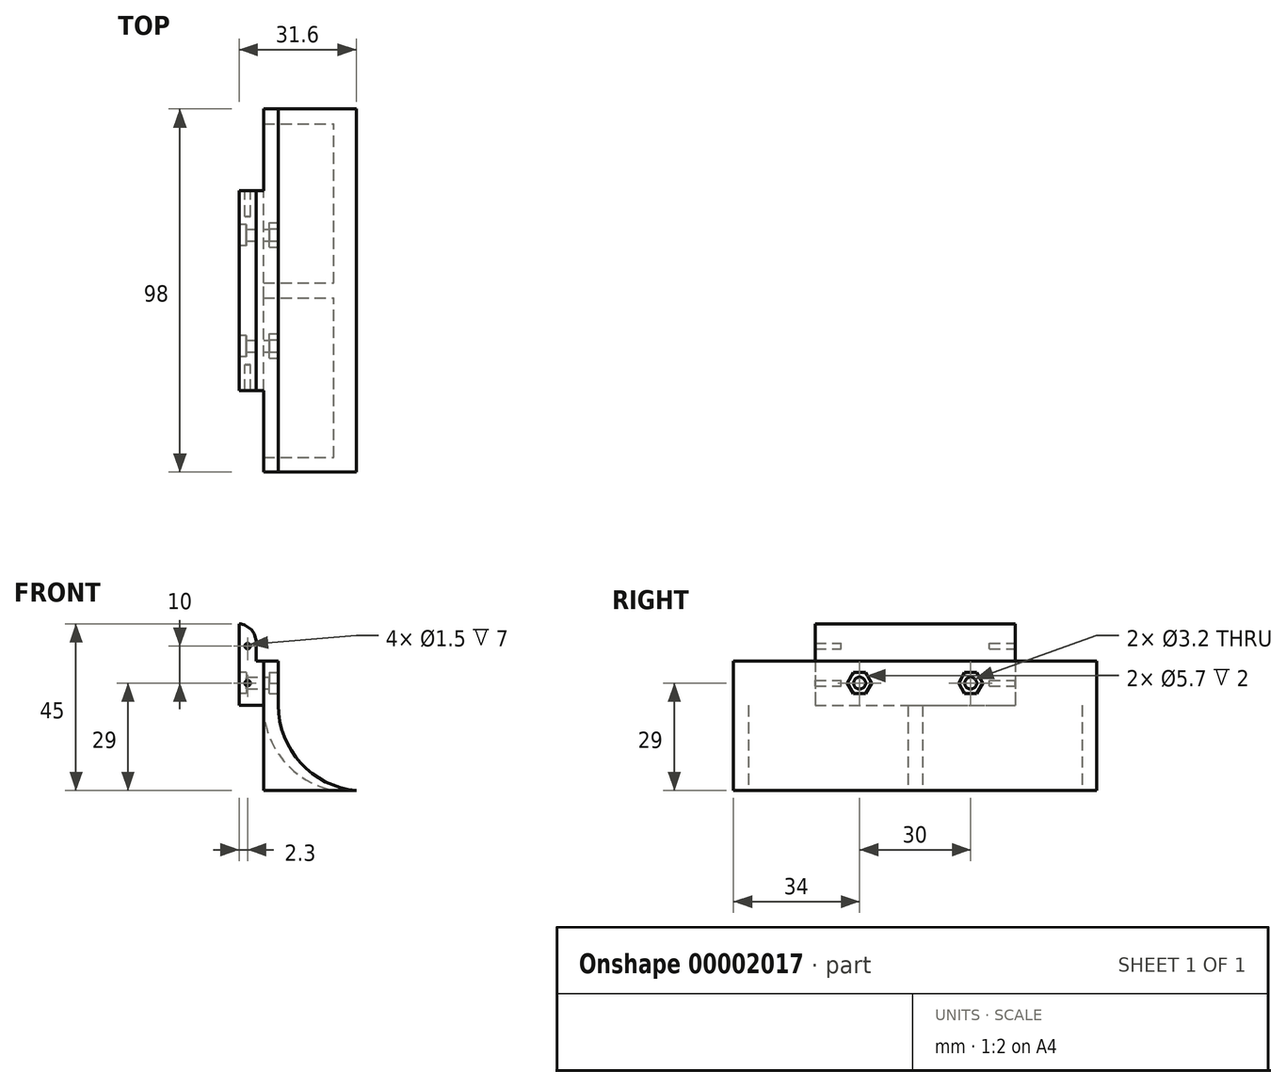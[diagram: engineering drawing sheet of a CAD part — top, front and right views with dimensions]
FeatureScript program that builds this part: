
annotation { "Feature Type Name" : "Feature", "Feature Type Description" : "" }
export const myFeature = defineFeature(function(context is Context, id is Id, definition is map)
    precondition{}
    {
        {
            var Q0;
            Q0=qCreatedBy(makeId("Front.planeOp"),FACE);
            var sketch = newSketch(context, id + "F0", { "sketchPlane" : qUnion([Q0])});
            skLineSegment(sketch, "E0", {"start": v(0, 0) * mm, "end": v(27, 0) * mm, "construction": true});
            skLineSegment(sketch, "E1", {"start": v(0, 0) * mm, "end": v(0, 35) * mm, "construction": true});
            skLineSegment(sketch, "E2", {"start": v(0, 35) * mm, "end": v(0, 45) * mm});
            skLineSegment(sketch, "E3", {"start": v(0, 45) * mm, "end": v(-4.6, 45) * mm});
            skLineSegment(sketch, "E4", {"start": v(-4.6, 45) * mm, "end": v(-4.6, 23) * mm});
            skLineSegment(sketch, "E5", {"start": v(-4.6, 23) * mm, "end": v(0, 23) * mm});
            skLineSegment(sketch, "E6", {"start": v(-2.3, 45) * mm, "end": v(-2.3, 23) * mm, "construction": true});
            skCircle(sketch, "E7", {"center": v(-2.3, 39) * mm, "radius": 0.75 * mm});
            skPoint(sketch, "E8", {"position": v(-2.3, 34) * mm});
            skCircle(sketch, "E9", {"center": v(-2.3, 29) * mm, "radius": 0.75 * mm});
            skLineSegment(sketch, "E10", {"start": v(0, 23) * mm, "end": v(6, 23) * mm});
            skLineSegment(sketch, "E11", {"start": v(6, 23) * mm, "end": v(6, 35) * mm});
            skLineSegment(sketch, "E12", {"start": v(6, 35) * mm, "end": v(0, 35) * mm});
            skArc(sketch, "E13", {"start": v(6, 23) * mm, "mid": v(12.04, 7.43) * mm, "end": v(27, 0) * mm});
            skLineSegment(sketch, "E14", {"start": v(2, 35) * mm, "end": v(2, 23) * mm});
            skLineSegment(sketch, "E15", {"start": v(2, 23) * mm, "end": v(2, 0) * mm});
            skLineSegment(sketch, "E16", {"start": v(2, 0) * mm, "end": v(27, 0) * mm});
            skArc(sketch, "E17", {"start": v(2, 23) * mm, "mid": v(7.36, 8.08) * mm, "end": v(21, 0) * mm});
            skSolve(sketch);
        }
        {
            var Q0;
            {var subQ2=sQuery(id+"F0.wireOp",EDGE,"E2");Q0=makeQuery(id+"F0.imprint","IMPRINT",FACE,{"disambiguationData":[TD([[makeQuery(id+"F0.imprint","IMPRINT",EDGE,{"derivedFrom":subQ2}),1.0]])]});}
            extrude(context, id + "F1", {"entities" : qUnion([Q0]), "endBound" : BoundingType.SYMMETRIC, "depth" : (27 * 2) * mm});
        }
        {
            var Q0;
            Q0=makeQuery(id+"F1.opExtrude","SWEPT_EDGE",EDGE,{"disambiguationData":[OSD([sQuery(id+"F0.wireOp",EDGE,"E2"),sQuery(id+"F0.wireOp",EDGE,"E3")])]});
            fillet(context, id + "F2", {"entities" : qUnion([Q0]), "radius" : 5 * mm, "tangentPropagation" : true, "allowEdgeOverflow" : false});
        }
        {
            var Q0;
            {var subQ2=sQuery(id+"F0.wireOp",EDGE,"E13");Q0=makeQuery(id+"F0.imprint","IMPRINT",FACE,{"disambiguationData":[TD([[makeQuery(id+"F0.imprint","IMPRINT",EDGE,{"derivedFrom":subQ2}),-1.0]])]});}
            var Q1;
            {var subQ2=sQuery(id+"F0.wireOp",EDGE,"E11");Q1=makeQuery(id+"F0.imprint","IMPRINT",FACE,{"disambiguationData":[TD([[makeQuery(id+"F0.imprint","IMPRINT",EDGE,{"derivedFrom":subQ2}),1.0]])]});}
            var Q2;
            {var subQ2=sQuery(id+"F0.wireOp",EDGE,"E15");Q2=makeQuery(id+"F0.imprint","IMPRINT",FACE,{"disambiguationData":[TD([[makeQuery(id+"F0.imprint","IMPRINT",EDGE,{"derivedFrom":subQ2}),1.0]])]});}
            extrude(context, id + "F3", {"entities" : qUnion([Q0, Q1, Q2]), "endBound" : BoundingType.SYMMETRIC, "depth" : 98 * mm});
        }
        {
            var Q0;
            {var subQ2=sQuery(id+"F0.wireOp",EDGE,"E15");Q0=makeQuery(id+"F0.imprint","IMPRINT",FACE,{"disambiguationData":[TD([[makeQuery(id+"F0.imprint","IMPRINT",EDGE,{"derivedFrom":subQ2}),1.0]])]});}
            extrude(context, id + "F4", {"entities" : qUnion([Q0]), "operationType" : NewBodyOperationType.REMOVE, "endBound" : BoundingType.SYMMETRIC, "depth" : 90 * mm});
        }
        {
            var Q0;
            Q0=makeQuery(id+"F0.imprint","IMPRINT",FACE,{"disambiguationData":[TD([[makeQuery(id+"F0.imprint","IMPRINT",EDGE,{"derivedFrom":sQuery(id+"F0.wireOp",EDGE,"E9")}),1.0]])]});
            var Q1;
            Q1=makeQuery(id+"F0.imprint","IMPRINT",FACE,{"disambiguationData":[TD([[makeQuery(id+"F0.imprint","IMPRINT",EDGE,{"derivedFrom":sQuery(id+"F0.wireOp",EDGE,"E7")}),1.0]])]});
            extrude(context, id + "F5", {"entities" : qUnion([Q0, Q1]), "operationType" : NewBodyOperationType.ADD, "endBound" : BoundingType.SYMMETRIC, "depth" : 40 * mm});
        }
        {
            var Q0;
            Q0=makeQuery(id+"F3.opExtrude","SWEPT_FACE",FACE,{"disambiguationData":[OSD([sQuery(id+"F0.wireOp",EDGE,"E11")])]});
            var sketch = newSketch(context, id + "F6", { "sketchPlane" : qUnion([Q0])});
            skLineSegment(sketch, "E18", {"start": v(0, 35) * mm, "end": v(0, 23) * mm, "construction": true});
            skPoint(sketch, "E19", {"position": v(0, 29) * mm});
            skCircle(sketch, "E20", {"center": v(-15, 29) * mm, "radius": 1.6 * mm});
            skCircle(sketch, "E21", {"center": v(15, 29) * mm, "radius": 1.6 * mm});
            skSolve(sketch);
        }
        {
            var Q0;
            Q0=makeQuery(id+"F6.imprint","IMPRINT",FACE,{"disambiguationData":[TD([[makeQuery(id+"F6.imprint","IMPRINT",EDGE,{"derivedFrom":sQuery(id+"F6.wireOp",EDGE,"E20")}),1.0]])]});
            var Q1;
            Q1=makeQuery(id+"F6.imprint","IMPRINT",FACE,{"disambiguationData":[TD([[makeQuery(id+"F6.imprint","IMPRINT",EDGE,{"derivedFrom":sQuery(id+"F6.wireOp",EDGE,"E21")}),1.0]])]});
            extrude(context, id + "F7", {"entities" : qUnion([Q0, Q1]), "operationType" : NewBodyOperationType.REMOVE, "endBound" : BoundingType.THROUGH_ALL, "oppositeDirection" : true, "depth" : 25 * mm});
        }
        {
            var Q0;
            {var subQ2=sQuery(id+"F0.wireOp",EDGE,"E15");Q0=makeQuery(id+"F0.imprint","IMPRINT",FACE,{"disambiguationData":[TD([[makeQuery(id+"F0.imprint","IMPRINT",EDGE,{"derivedFrom":subQ2}),1.0]])]});}
            extrude(context, id + "F8", {"entities" : qUnion([Q0]), "operationType" : NewBodyOperationType.ADD, "endBound" : BoundingType.SYMMETRIC, "depth" : 4 * mm});
        }
        {
            var Q0;
            Q0=makeQuery(id+"F3.opExtrude","SWEPT_FACE",FACE,{"disambiguationData":[OSD([sQuery(id+"F0.wireOp",EDGE,"E11")])]});
            var sketch = newSketch(context, id + "F9", { "sketchPlane" : qUnion([Q0])});
            skCircle(sketch, "E22.cCircle", {"center": v(-15, 29) * mm, "radius": 2.85 * mm, "construction": true});
            skLineSegment(sketch, "E22.0", {"start": v(-13.35, 31.85) * mm, "end": v(-11.7, 29) * mm});
            skLineSegment(sketch, "E22.1", {"start": v(-11.7, 29) * mm, "end": v(-13.35, 26.15) * mm});
            skLineSegment(sketch, "E22.2", {"start": v(-13.35, 26.15) * mm, "end": v(-16.65, 26.15) * mm});
            skLineSegment(sketch, "E22.3", {"start": v(-16.65, 26.15) * mm, "end": v(-18.3, 29) * mm});
            skLineSegment(sketch, "E22.4", {"start": v(-18.3, 29) * mm, "end": v(-16.65, 31.85) * mm});
            skLineSegment(sketch, "E22.5", {"start": v(-16.65, 31.85) * mm, "end": v(-13.35, 31.85) * mm});
            skPoint(sketch, "E22.0.midPoint", {"position": v(-12.53, 30.43) * mm});
            skCircle(sketch, "E23.cCircle", {"center": v(15, 29) * mm, "radius": 2.85 * mm, "construction": true});
            skLineSegment(sketch, "E23.0", {"start": v(16.65, 31.85) * mm, "end": v(18.3, 29) * mm});
            skLineSegment(sketch, "E23.1", {"start": v(18.3, 29) * mm, "end": v(16.65, 26.15) * mm});
            skLineSegment(sketch, "E23.2", {"start": v(16.65, 26.15) * mm, "end": v(13.35, 26.15) * mm});
            skLineSegment(sketch, "E23.3", {"start": v(13.35, 26.15) * mm, "end": v(11.7, 29) * mm});
            skLineSegment(sketch, "E23.4", {"start": v(11.7, 29) * mm, "end": v(13.35, 31.85) * mm});
            skLineSegment(sketch, "E23.5", {"start": v(13.35, 31.85) * mm, "end": v(16.65, 31.85) * mm});
            skPoint(sketch, "E23.0.midPoint", {"position": v(17.47, 30.43) * mm});
            skSolve(sketch);
        }
        {
            var Q0;
            Q0=makeQuery(id+"F9.imprint","IMPRINT",FACE,{"disambiguationData":[TD([[makeQuery(id+"F9.imprint","IMPRINT",EDGE,{"derivedFrom":sQuery(id+"F9.wireOp",EDGE,"E22.0")}),-1.0]])]});
            var Q1;
            Q1=makeQuery(id+"F9.imprint","IMPRINT",FACE,{"disambiguationData":[TD([[makeQuery(id+"F9.imprint","IMPRINT",EDGE,{"derivedFrom":sQuery(id+"F9.wireOp",EDGE,"E23.0")}),-1.0]])]});
            extrude(context, id + "F10", {"entities" : qUnion([Q0, Q1]), "operationType" : NewBodyOperationType.REMOVE, "oppositeDirection" : true, "depth" : 2.5 * mm});
        }
        {
            var Q0;
            Q0=makeQuery(id+"F1.opExtrude","SWEPT_FACE",FACE,{"disambiguationData":[OSD([sQuery(id+"F0.wireOp",EDGE,"E4")])]});
            var sketch = newSketch(context, id + "F11", { "sketchPlane" : qUnion([Q0])});
            skCircle(sketch, "E24", {"center": v(-15, 29) * mm, "radius": 2.85 * mm});
            skCircle(sketch, "E25", {"center": v(15, 29) * mm, "radius": 2.85 * mm});
            skSolve(sketch);
        }
        {
            var Q0;
            Q0=makeQuery(id+"F11.imprint","IMPRINT",FACE,{"disambiguationData":[TD([[makeQuery(id+"F11.imprint","IMPRINT",EDGE,{"derivedFrom":sQuery(id+"F11.wireOp",EDGE,"E24")}),1.0]])]});
            var Q1;
            Q1=makeQuery(id+"F11.imprint","IMPRINT",FACE,{"disambiguationData":[TD([[makeQuery(id+"F11.imprint","IMPRINT",EDGE,{"derivedFrom":sQuery(id+"F11.wireOp",EDGE,"E25")}),1.0]])]});
            extrude(context, id + "F12", {"entities" : qUnion([Q0, Q1]), "operationType" : NewBodyOperationType.REMOVE, "oppositeDirection" : true, "depth" : 2 * mm});
        }
    });
